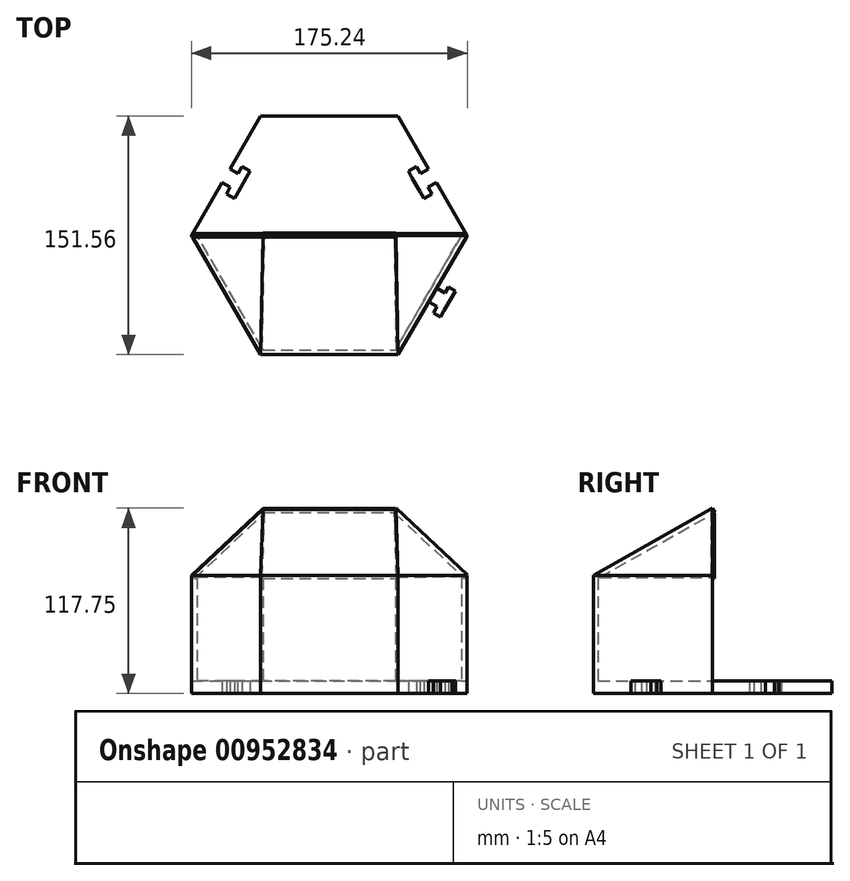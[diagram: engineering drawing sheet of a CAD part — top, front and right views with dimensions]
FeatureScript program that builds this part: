
annotation { "Feature Type Name" : "Feature", "Feature Type Description" : "" }
export const myFeature = defineFeature(function(context is Context, id is Id, definition is map)
    precondition{}
    {
        {
            var Q0;
            Q0=qCreatedBy(makeId("Top.planeOp"),FACE);
            var sketch = newSketch(context, id + "F0", { "sketchPlane" : qUnion([Q0])});
            skCircle(sketch, "E0.cCircle", {"center": v(0, 0) * mm, "radius": 75.78 * mm, "construction": true});
            skLineSegment(sketch, "E0.0", {"start": v(-43.75, 75.78) * mm, "end": v(43.75, 75.78) * mm});
            skLineSegment(sketch, "E0.1", {"start": v(43.75, 75.78) * mm, "end": v(87.5, 0) * mm});
            skLineSegment(sketch, "E0.2", {"start": v(87.5, 0) * mm, "end": v(43.75, -75.78) * mm});
            skLineSegment(sketch, "E0.3", {"start": v(43.75, -75.78) * mm, "end": v(-43.75, -75.78) * mm});
            skLineSegment(sketch, "E0.4", {"start": v(-43.75, -75.78) * mm, "end": v(-87.5, 0) * mm});
            skLineSegment(sketch, "E0.5", {"start": v(-87.5, 0) * mm, "end": v(-43.75, 75.78) * mm});
            skPoint(sketch, "E0.0.midPoint", {"position": v(0, 75.78) * mm});
            skLineSegment(sketch, "E1.0", {"start": v(-84.04, 0) * mm, "end": v(-42.02, 72.78) * mm});
            skLineSegment(sketch, "E1.1", {"start": v(42.02, 72.78) * mm, "end": v(84.04, 0) * mm});
            skLineSegment(sketch, "E1.2", {"start": v(84.04, 0) * mm, "end": v(42.02, -72.78) * mm});
            skLineSegment(sketch, "E1.3", {"start": v(-42.02, 72.78) * mm, "end": v(42.02, 72.78) * mm});
            skLineSegment(sketch, "E1.4", {"start": v(42.02, -72.78) * mm, "end": v(-42.02, -72.78) * mm});
            skLineSegment(sketch, "E1.5", {"start": v(-42.02, -72.78) * mm, "end": v(-84.04, 0) * mm});
            skLineSegment(sketch, "E2", {"start": v(-87.5, 0) * mm, "end": v(-84.04, 0) * mm});
            skLineSegment(sketch, "E3", {"start": v(84.04, 0) * mm, "end": v(87.5, 0) * mm});
            skLineSegment(sketch, "E4", {"start": v(0, 0) * mm, "end": v(0, 72.78) * mm, "construction": true});
            skLineSegment(sketch, "E5", {"start": v(0, 0) * mm, "end": v(42.02, 72.78) * mm, "construction": true});
            skLineSegment(sketch, "E6", {"start": v(0, 0) * mm, "end": v(-42.02, 72.78) * mm, "construction": true});
            skLineSegment(sketch, "E7", {"start": v(0, 36.39) * mm, "end": v(0, 72.78) * mm, "construction": true});
            skLineSegment(sketch, "E8.bottom", {"start": v(25, 48.33) * mm, "end": v(-25, 48.33) * mm});
            skLineSegment(sketch, "E8.top", {"start": v(25, 60.83) * mm, "end": v(-25, 60.83) * mm});
            skLineSegment(sketch, "E8.left", {"start": v(25, 48.33) * mm, "end": v(25, 60.83) * mm});
            skLineSegment(sketch, "E8.right", {"start": v(-25, 48.33) * mm, "end": v(-25, 60.83) * mm});
            skPoint(sketch, "E8.middle", {"position": v(0, 54.58) * mm});
            skLineSegment(sketch, "E9", {"start": v(-65.63, 37.89) * mm, "end": v(-55.16, 32) * mm, "construction": true});
            skLineSegment(sketch, "E10", {"start": v(-55.16, 32) * mm, "end": v(-52.71, 36.37) * mm, "construction": true});
            skLineSegment(sketch, "E11", {"start": v(-55.16, 32) * mm, "end": v(-57.62, 27.65) * mm, "construction": true});
            skLineSegment(sketch, "E12", {"start": v(-52.71, 36.37) * mm, "end": v(-63.12, 42.22) * mm});
            skLineSegment(sketch, "E13", {"start": v(-57.62, 27.65) * mm, "end": v(-52.71, 36.37) * mm});
            skLineSegment(sketch, "E14", {"start": v(-65.63, 37.89) * mm, "end": v(-68.13, 33.56) * mm});
            skLineSegment(sketch, "E15", {"start": v(-57.62, 27.65) * mm, "end": v(-68.13, 33.56) * mm});
            skLineSegment(sketch, "E16.MirrorCS", {"start": v(55.16, 32) * mm, "end": v(57.62, 27.65) * mm});
            skLineSegment(sketch, "E17.MirrorCS", {"start": v(55.16, 32) * mm, "end": v(52.71, 36.37) * mm});
            skLineSegment(sketch, "E18.MirrorCS", {"start": v(57.62, 27.65) * mm, "end": v(68.13, 33.56) * mm});
            skLineSegment(sketch, "E19.MirrorCS", {"start": v(87.5, 0) * mm, "end": v(43.75, 75.78) * mm});
            skLineSegment(sketch, "E20.MirrorCS", {"start": v(52.71, 36.37) * mm, "end": v(63.12, 42.22) * mm});
            skLineSegment(sketch, "E21", {"start": v(-62.87, 30.6) * mm, "end": v(-65.32, 26.25) * mm});
            skLineSegment(sketch, "E22", {"start": v(-57.62, 27.65) * mm, "end": v(-60.07, 23.3) * mm});
            skLineSegment(sketch, "E23", {"start": v(-65.32, 26.25) * mm, "end": v(-60.07, 23.3) * mm});
            skLineSegment(sketch, "E24.MirrorCS", {"start": v(-52.71, 36.37) * mm, "end": v(-50.26, 40.72) * mm});
            skLineSegment(sketch, "E25.MirrorCS", {"start": v(-57.97, 39.32) * mm, "end": v(-55.52, 43.68) * mm});
            skLineSegment(sketch, "E26.MirrorCS", {"start": v(-55.52, 43.68) * mm, "end": v(-50.26, 40.72) * mm});
            skLineSegment(sketch, "E27.MirrorCS", {"start": v(57.97, 39.32) * mm, "end": v(55.52, 43.68) * mm});
            skLineSegment(sketch, "E28.MirrorCS", {"start": v(55.52, 43.68) * mm, "end": v(50.26, 40.72) * mm});
            skLineSegment(sketch, "E29.MirrorCS", {"start": v(52.71, 36.37) * mm, "end": v(50.26, 40.72) * mm});
            skLineSegment(sketch, "E30.MirrorCS", {"start": v(57.62, 27.65) * mm, "end": v(60.07, 23.3) * mm});
            skLineSegment(sketch, "E31.MirrorCS", {"start": v(62.87, 30.6) * mm, "end": v(65.32, 26.25) * mm});
            skLineSegment(sketch, "E32.MirrorCS", {"start": v(65.32, 26.25) * mm, "end": v(60.07, 23.3) * mm});
            skLineSegment(sketch, "E33.MirrorCS", {"start": v(68.6, -45.34) * mm, "end": v(66.35, -49.24) * mm});
            skLineSegment(sketch, "E34.MirrorCS", {"start": v(66.35, -49.24) * mm, "end": v(70.68, -51.74) * mm});
            skLineSegment(sketch, "E35.MirrorCS", {"start": v(72.93, -47.84) * mm, "end": v(70.68, -51.74) * mm});
            skLineSegment(sketch, "E36.MirrorCS", {"start": v(72.93, -47.84) * mm, "end": v(63.14, -42.19) * mm});
            skLineSegment(sketch, "E37.MirrorCS", {"start": v(77.93, -39.18) * mm, "end": v(72.93, -47.84) * mm});
            skLineSegment(sketch, "E38.MirrorCS", {"start": v(77.93, -39.18) * mm, "end": v(68.14, -33.53) * mm});
            skLineSegment(sketch, "E39.MirrorCS", {"start": v(73.6, -36.68) * mm, "end": v(75.74, -32.72) * mm});
            skLineSegment(sketch, "E40.MirrorCS", {"start": v(75.74, -32.72) * mm, "end": v(80.12, -35.25) * mm});
            skLineSegment(sketch, "E41.MirrorCS", {"start": v(77.93, -39.18) * mm, "end": v(80.12, -35.25) * mm});
            skLineSegment(sketch, "E42", {"start": v(-68.13, 33.56) * mm, "end": v(-65.5, 32.09) * mm});
            skLineSegment(sketch, "E43", {"start": v(68.13, 33.56) * mm, "end": v(65.5, 32.09) * mm});
            skSolve(sketch);
        }
        {
            var Q0;
            Q0=makeQuery(id+"F0.imprint","IMPRINT",FACE,{"disambiguationData":[TD([[makeQuery(id+"F0.imprint","IMPRINT",EDGE,{"derivedFrom":sQuery(id+"F0.wireOp",EDGE,"E1.0")}),-1.0]])]});
            extrude(context, id + "F1", {"entities" : qUnion([Q0]), "depth" : 8 * mm, "offsetDistance" : 25 * mm});
        }
        {
            var Q0;
            Q0=makeQuery(id+"F0.imprint","IMPRINT",FACE,{"disambiguationData":[TD([[makeQuery(id+"F0.imprint","IMPRINT",EDGE,{"derivedFrom":sQuery(id+"F0.wireOp",EDGE,"E0.2")}),-1.0]])]});
            extrude(context, id + "F2", {"entities" : qUnion([Q0]), "operationType" : NewBodyOperationType.ADD, "depth" : 75 * mm, "offsetDistance" : 25 * mm});
        }
        {
            var Q0;
            Q0=qCreatedBy(makeId("Front.planeOp"),FACE);
            var sketch = newSketch(context, id + "F3", { "sketchPlane" : qUnion([Q0])});
            skLineSegment(sketch, "E44", {"start": v(0, 0) * mm, "end": v(0, 144.27) * mm, "construction": true});
            skLineSegment(sketch, "E45", {"start": v(0, 144.27) * mm, "end": v(-94, 144.27) * mm, "construction": true});
            skLineSegment(sketch, "E46", {"start": v(0, 144.27) * mm, "end": v(81.74, 144.27) * mm});
            skLineSegment(sketch, "E47", {"start": v(0, 0) * mm, "end": v(0, 75) * mm, "construction": true});
            skLineSegment(sketch, "E48", {"start": v(0, 75) * mm, "end": v(0, 114.5) * mm, "construction": true});
            skLineSegment(sketch, "E49", {"start": v(0, 75) * mm, "end": v(-87.5, 75) * mm, "construction": true});
            skLineSegment(sketch, "E50", {"start": v(0, 114.5) * mm, "end": v(42.02, 114.5) * mm, "construction": true});
            skLineSegment(sketch, "E51", {"start": v(0, 114.5) * mm, "end": v(-42.02, 114.5) * mm});
            skLineSegment(sketch, "E52", {"start": v(0, 75) * mm, "end": v(-84.04, 75) * mm, "construction": true});
            skLineSegment(sketch, "E53", {"start": v(-42.02, 114.5) * mm, "end": v(-84.04, 75) * mm});
            skLineSegment(sketch, "E54", {"start": v(-42.02, 114.5) * mm, "end": v(-42.02, 117.5) * mm, "construction": true});
            skLineSegment(sketch, "E55", {"start": v(-42.02, 117.5) * mm, "end": v(-87.5, 75) * mm});
            skLineSegment(sketch, "E56", {"start": v(-42.02, 117.5) * mm, "end": v(0, 117.5) * mm});
            skLineSegment(sketch, "E57.MirrorCS", {"start": v(42.02, 117.5) * mm, "end": v(87.5, 75) * mm});
            skLineSegment(sketch, "E58.MirrorCS", {"start": v(42.02, 114.5) * mm, "end": v(84.04, 75) * mm});
            skLineSegment(sketch, "E59.MirrorCS", {"start": v(42.02, 117.5) * mm, "end": v(0, 117.5) * mm});
            skLineSegment(sketch, "E60.MirrorCS", {"start": v(0, 114.5) * mm, "end": v(42.02, 114.5) * mm});
            skLineSegment(sketch, "E61", {"start": v(87.5, 75) * mm, "end": v(84.04, 75) * mm});
            skLineSegment(sketch, "E62", {"start": v(-84.04, 75) * mm, "end": v(-87.5, 75) * mm});
            skSolve(sketch);
        }
        {
            var Q0;
            Q0=makeQuery(id+"F0.imprint","IMPRINT",FACE,{"disambiguationData":[TD([[makeQuery(id+"F0.imprint","IMPRINT",EDGE,{"derivedFrom":sQuery(id+"F0.wireOp",EDGE,"E0.0")}),-1.0]])]});
            extrude(context, id + "F4", {"entities" : qUnion([Q0]), "operationType" : NewBodyOperationType.ADD, "oppositeDirection" : true, "depth" : -8 * mm, "offsetDistance" : 25 * mm});
        }
        {
            var Q0;
            Q0=makeQuery(id+"F2.opExtrude","CAP_EDGE",EDGE,{"disambiguationData":[OSD([sQuery(id+"F0.wireOp",EDGE,"E0.3")])],"isStart":false});
            var Q1;
            Q1=sQuery(id+"F3.wireOp",VERTEX,"E56.end");
            cPlane(context, id + "F5", {"entities" : qUnion([Q0, Q1]), "cplaneType" : CPlaneType.LINE_ANGLE, "offset" : 25 * mm, "angle" : 0 * degree, "width" : 150 * mm, "height" : 150 * mm});
        }
        {
            var Q0;
            Q0=qCreatedBy(id+"F5.planeOp",FACE);
            var sketch = newSketch(context, id + "F6", { "sketchPlane" : qUnion([Q0])});
            skLineSegment(sketch, "E63", {"start": v(0, 29.4) * mm, "end": v(43.75, 29.4) * mm});
            skLineSegment(sketch, "E64", {"start": v(0, 29.4) * mm, "end": v(-43.75, 29.4) * mm});
            skLineSegment(sketch, "E65", {"start": v(-43.75, 29.4) * mm, "end": v(-42.02, -57.48) * mm});
            skLineSegment(sketch, "E66", {"start": v(43.75, 29.4) * mm, "end": v(42.02, -57.48) * mm});
            skLineSegment(sketch, "E67", {"start": v(-42.02, -57.48) * mm, "end": v(42.02, -57.48) * mm});
            skSolve(sketch);
        }
        {
            var Q0;
            Q0=makeQuery(id+"F6.imprint","IMPRINT",FACE,{"disambiguationData":[TD([[makeQuery(id+"F6.imprint","IMPRINT",EDGE,{"derivedFrom":sQuery(id+"F6.wireOp",EDGE,"E63")}),-1.0]])]});
            extrude(context, id + "F7", {"entities" : qUnion([Q0]), "operationType" : NewBodyOperationType.ADD, "depth" : 3 * mm, "offsetDistance" : 25 * mm});
        }
        {
            var Q0;
            Q0=makeQuery(id+"F3.imprint","IMPRINT",FACE,{"disambiguationData":[TD([[makeQuery(id+"F3.imprint","IMPRINT",EDGE,{"derivedFrom":sQuery(id+"F3.wireOp",EDGE,"E51")}),-1.0]])]});
            extrude(context, id + "F8", {"entities" : qUnion([Q0]), "operationType" : NewBodyOperationType.ADD, "depth" : 1 * mm, "offsetDistance" : 25 * mm});
        }
        {
            var Q0;
            Q0=makeQuery(id+"F8.opExtrude","CAP_EDGE",EDGE,{"disambiguationData":[OSD([sQuery(id+"F3.wireOp",EDGE,"E55")])],"isStart":true});
            var Q1;
            Q1=makeQuery(id+"F7.boolean.opBoolean","MERGE",VERTEX,{"derivedFrom":[makeQuery(id+"F2.opExtrude","CAP_VERTEX",VERTEX,{"disambiguationData":[OSD([sQuery(id+"F0.wireOp",EDGE,"E0.3"),sQuery(id+"F0.wireOp",EDGE,"E0.4")])],"isStart":false}),makeQuery(id+"F7.opExtrude","CAP_VERTEX",VERTEX,{"disambiguationData":[OSD([sQuery(id+"F6.wireOp",EDGE,"E64"),sQuery(id+"F6.wireOp",EDGE,"E65")])],"isStart":true})]});
            cPlane(context, id + "F9", {"entities" : qUnion([Q0, Q1]), "cplaneType" : CPlaneType.LINE_ANGLE, "offset" : 25 * mm, "angle" : 0 * degree, "width" : 150 * mm, "height" : 150 * mm});
        }
        {
            var Q0;
            Q0=qCreatedBy(id+"F9.planeOp",FACE);
            var sketch = newSketch(context, id + "F10", { "sketchPlane" : qUnion([Q0])});
            skLineSegment(sketch, "E68", {"start": v(-25.66, 35.61) * mm, "end": v(30.99, -31.08) * mm});
            skLineSegment(sketch, "E69", {"start": v(-25.66, 35.61) * mm, "end": v(33.23, 55.79) * mm});
            skLineSegment(sketch, "E70", {"start": v(33.23, 55.79) * mm, "end": v(30.99, -31.08) * mm});
            skSolve(sketch);
        }
        {
            var Q0;
            Q0=qSketchRegion(id+"F10",true);
            extrude(context, id + "F11", {"entities" : qUnion([Q0]), "operationType" : NewBodyOperationType.ADD, "depth" : -3 * mm, "offsetDistance" : 25 * mm});
        }
        {
            var Q0;
            Q0=makeQuery(id+"F8.opExtrude","CAP_EDGE",EDGE,{"disambiguationData":[OSD([sQuery(id+"F3.wireOp",EDGE,"E57.MirrorCS")])],"isStart":false});
            var Q1;
            Q1=makeQuery(id+"F7.boolean.opBoolean","MERGE",VERTEX,{"derivedFrom":[makeQuery(id+"F2.opExtrude","CAP_VERTEX",VERTEX,{"disambiguationData":[OSD([sQuery(id+"F0.wireOp",EDGE,"E0.2"),sQuery(id+"F0.wireOp",EDGE,"E0.3")])],"isStart":false}),makeQuery(id+"F7.opExtrude","CAP_VERTEX",VERTEX,{"disambiguationData":[OSD([sQuery(id+"F6.wireOp",EDGE,"E63"),sQuery(id+"F6.wireOp",EDGE,"E66")])],"isStart":true})]});
            cPlane(context, id + "F12", {"entities" : qUnion([Q0, Q1]), "cplaneType" : CPlaneType.LINE_ANGLE, "offset" : 25 * mm, "angle" : 0 * degree, "width" : 150 * mm, "height" : 150 * mm});
        }
        {
            var Q0;
            Q0=qCreatedBy(id+"F12.planeOp",FACE);
            var sketch = newSketch(context, id + "F13", { "sketchPlane" : qUnion([Q0])});
            skLineSegment(sketch, "E71", {"start": v(-32.88, -56.36) * mm, "end": v(25.94, -35.98) * mm});
            skLineSegment(sketch, "E72", {"start": v(25.94, -35.98) * mm, "end": v(-30.94, 30.51) * mm});
            skLineSegment(sketch, "E73", {"start": v(-30.94, 30.51) * mm, "end": v(-32.88, -56.36) * mm});
            skSolve(sketch);
        }
        {
            var Q0;
            Q0=qSketchRegion(id+"F13",true);
            extrude(context, id + "F14", {"entities" : qUnion([Q0]), "operationType" : NewBodyOperationType.ADD, "depth" : 3 * mm, "offsetDistance" : 25 * mm});
        }
        {
            var Q0;
            Q0=makeQuery(id+"F0.imprint","IMPRINT",FACE,{"disambiguationData":[TD([[makeQuery(id+"F0.imprint","IMPRINT",EDGE,{"derivedFrom":sQuery(id+"F0.wireOp",EDGE,"E8.bottom")}),-1.0]])]});
            extrude(context, id + "F15", {"entities" : qUnion([Q0]), "operationType" : NewBodyOperationType.ADD, "depth" : 8 * mm, "offsetDistance" : 25 * mm});
        }
        {
            var Q0;
            {var subQ5=sQuery(id+"F0.wireOp",EDGE,"749d55a2-1ae5-4b90-8efe-ab6072e4ac770.MirrorCS");Q0=makeQuery(id+"F0.imprint","IMPRINT",FACE,{"disambiguationData":[TD([[makeQuery(id+"F0.imprint","IMPRINT",EDGE,{"derivedFrom":subQ5}),1.0]])]});}
            var Q1;
            {var subQ4=sQuery(id+"F0.wireOp",EDGE,"bf9a6782-c77d-4324-b6f4-6efb0bd9360c0.MirrorCS");Q1=makeQuery(id+"F0.imprint","IMPRINT",FACE,{"disambiguationData":[TD([[makeQuery(id+"F0.imprint","IMPRINT",EDGE,{"derivedFrom":subQ4}),1.0]])]});}
            var Q2;
            {var subQ0=sQuery(id+"F0.wireOp",EDGE,"c1ebaf2c-39ee-4834-980c-edcd090fc9720.MirrorCS");Q2=makeQuery(id+"F0.imprint","IMPRINT",FACE,{"disambiguationData":[TD([[makeQuery(id+"F0.imprint","IMPRINT",EDGE,{"derivedFrom":subQ0}),1.0]])]});}
            var Q3;
            {var subQ5=sQuery(id+"F0.wireOp",EDGE,"E40.MirrorCS");Q3=makeQuery(id+"F0.imprint","IMPRINT",FACE,{"disambiguationData":[TD([[makeQuery(id+"F0.imprint","IMPRINT",EDGE,{"derivedFrom":subQ5}),-1.0]])]});}
            var Q4;
            {var subQ0=sQuery(id+"F0.wireOp",EDGE,"E37.MirrorCS");Q4=makeQuery(id+"F0.imprint","IMPRINT",FACE,{"disambiguationData":[TD([[makeQuery(id+"F0.imprint","IMPRINT",EDGE,{"derivedFrom":subQ0}),-1.0]])]});}
            var Q5;
            {var subQ0=sQuery(id+"F0.wireOp",EDGE,"E33.MirrorCS");Q5=makeQuery(id+"F0.imprint","IMPRINT",FACE,{"disambiguationData":[TD([[makeQuery(id+"F0.imprint","IMPRINT",EDGE,{"derivedFrom":subQ0}),1.0]])]});}
            extrude(context, id + "F16", {"entities" : qUnion([Q0, Q1, Q2, Q3, Q4, Q5]), "operationType" : NewBodyOperationType.ADD, "depth" : 8 * mm, "offsetDistance" : 25 * mm});
        }
        {
            var Q0;
            {var subQ0=sQuery(id+"F0.wireOp",EDGE,"E2");Q0=makeQuery(id+"F0.imprint","IMPRINT",FACE,{"disambiguationData":[TD([[makeQuery(id+"F0.imprint","IMPRINT",EDGE,{"derivedFrom":subQ0}),1.0]])]});}
            extrude(context, id + "F17", {"entities" : qUnion([Q0]), "operationType" : NewBodyOperationType.ADD, "depth" : 8 * mm, "offsetDistance" : 25 * mm});
        }
        {
            var Q0;
            {var subQ0=sQuery(id+"F0.wireOp",EDGE,"E3");Q0=makeQuery(id+"F0.imprint","IMPRINT",FACE,{"disambiguationData":[TD([[makeQuery(id+"F0.imprint","IMPRINT",EDGE,{"derivedFrom":subQ0}),1.0]])]});}
            extrude(context, id + "F18", {"entities" : qUnion([Q0]), "operationType" : NewBodyOperationType.ADD, "depth" : 8 * mm, "offsetDistance" : 25 * mm});
        }
    });
